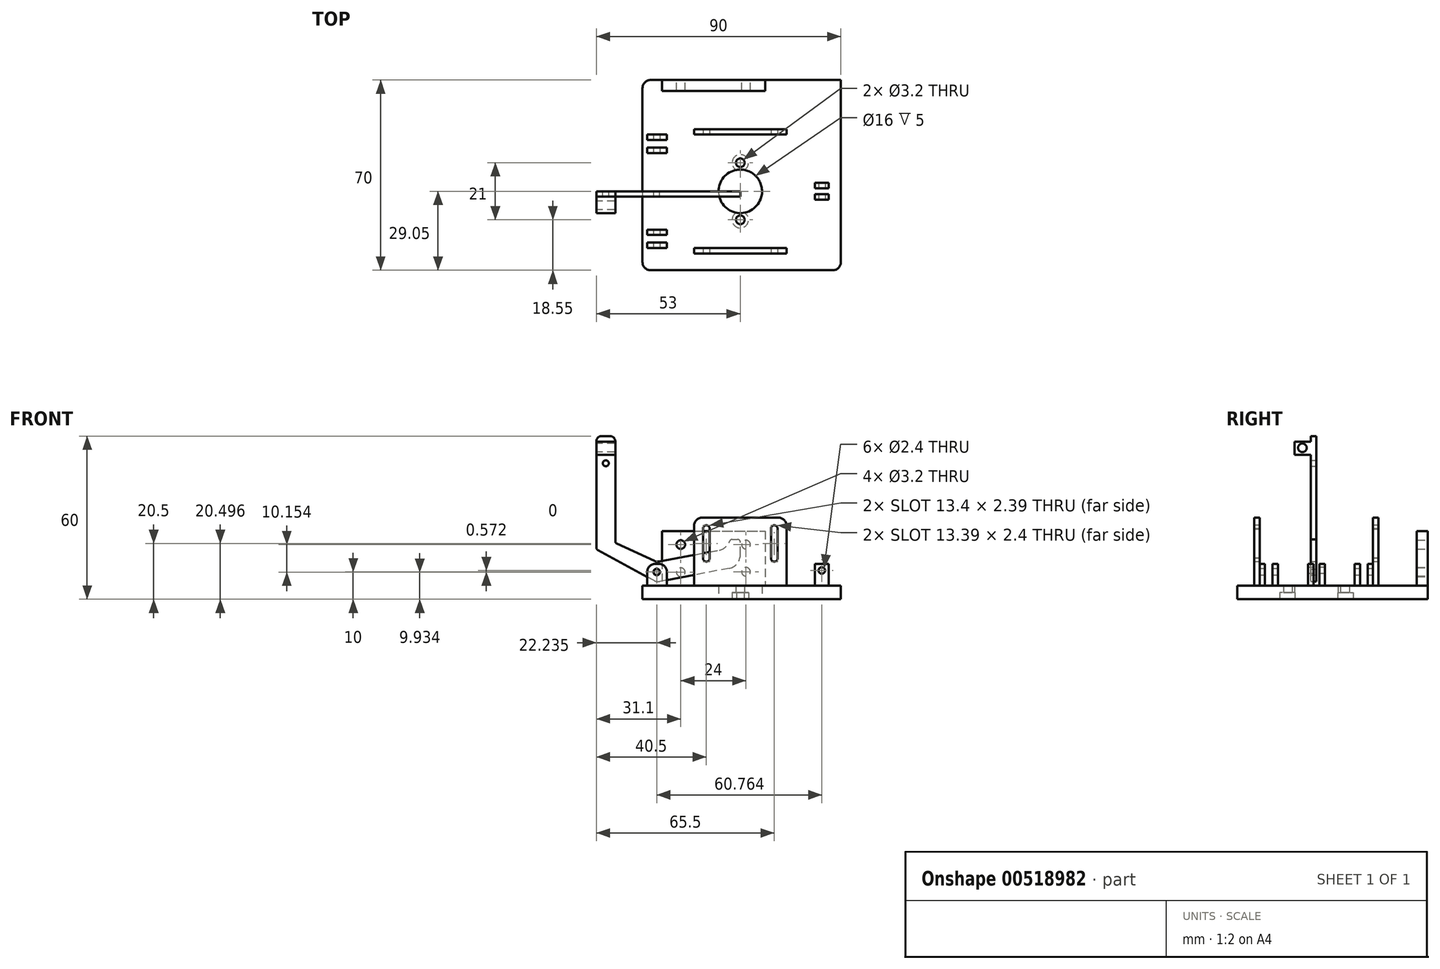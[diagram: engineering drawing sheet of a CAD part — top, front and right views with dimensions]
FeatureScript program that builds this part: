
annotation { "Feature Type Name" : "Feature", "Feature Type Description" : "" }
export const myFeature = defineFeature(function(context is Context, id is Id, definition is map)
    precondition{}
    {
        {
            var Q0;
            Q0=qCreatedBy(makeId("Top.planeOp"),FACE);
            var sketch = newSketch(context, id + "F0", { "sketchPlane" : qUnion([Q0])});
            skLineSegment(sketch, "E0.bottom", {"start": v(-36, 40.95) * mm, "end": v(37, 40.95) * mm});
            skLineSegment(sketch, "E0.top", {"start": v(-36, -29.05) * mm, "end": v(37, -29.05) * mm});
            skLineSegment(sketch, "E0.left", {"start": v(-36, 40.95) * mm, "end": v(-36, -29.05) * mm});
            skLineSegment(sketch, "E0.right", {"start": v(37, 40.95) * mm, "end": v(37, -29.05) * mm});
            skCircle(sketch, "E1.cCircle", {"center": v(0, 22.5) * mm, "radius": 2.85 * mm, "construction": true});
            skLineSegment(sketch, "E1.0", {"start": v(2.85, 20.85) * mm, "end": v(0, 19.2) * mm});
            skLineSegment(sketch, "E1.1", {"start": v(0, 19.2) * mm, "end": v(-2.85, 20.85) * mm});
            skLineSegment(sketch, "E1.2", {"start": v(-2.85, 20.85) * mm, "end": v(-2.85, 24.15) * mm});
            skLineSegment(sketch, "E1.3", {"start": v(-2.85, 24.15) * mm, "end": v(0, 25.8) * mm});
            skLineSegment(sketch, "E1.4", {"start": v(0, 25.8) * mm, "end": v(2.85, 24.15) * mm});
            skLineSegment(sketch, "E1.5", {"start": v(2.85, 24.15) * mm, "end": v(2.85, 20.85) * mm});
            skPoint(sketch, "E1.0.midPoint", {"position": v(1.43, 20.03) * mm});
            skCircle(sketch, "E2.cCircle", {"center": v(0, -22.5) * mm, "radius": 2.85 * mm, "construction": true});
            skLineSegment(sketch, "E2.0", {"start": v(2.85, -24.15) * mm, "end": v(0, -25.8) * mm});
            skLineSegment(sketch, "E2.1", {"start": v(0, -25.8) * mm, "end": v(-2.85, -24.15) * mm});
            skLineSegment(sketch, "E2.2", {"start": v(-2.85, -24.15) * mm, "end": v(-2.85, -20.85) * mm});
            skLineSegment(sketch, "E2.3", {"start": v(-2.85, -20.85) * mm, "end": v(0, -19.2) * mm});
            skLineSegment(sketch, "E2.4", {"start": v(0, -19.2) * mm, "end": v(2.85, -20.85) * mm});
            skLineSegment(sketch, "E2.5", {"start": v(2.85, -20.85) * mm, "end": v(2.85, -24.15) * mm});
            skPoint(sketch, "E2.0.midPoint", {"position": v(1.43, -24.97) * mm});
            skCircle(sketch, "E3", {"center": v(0, 22.5) * mm, "radius": 1.6 * mm});
            skCircle(sketch, "E4", {"center": v(0, -22.5) * mm, "radius": 1.6 * mm});
            skCircle(sketch, "E5", {"center": v(0, 0) * mm, "radius": 8 * mm});
            skLineSegment(sketch, "E6", {"start": v(0, 22.5) * mm, "end": v(0, 0) * mm, "construction": true});
            skLineSegment(sketch, "E7", {"start": v(0, 0) * mm, "end": v(0, -22.5) * mm, "construction": true});
            skCircle(sketch, "E8", {"center": v(0, 10.5) * mm, "radius": 3 * mm});
            skCircle(sketch, "E9", {"center": v(0, -10.5) * mm, "radius": 3 * mm});
            skPoint(sketch, "E10", {"position": v(0, 11.25) * mm});
            skCircle(sketch, "E11", {"center": v(0, 10.5) * mm, "radius": 1.6 * mm});
            skCircle(sketch, "E12", {"center": v(0, -10.5) * mm, "radius": 1.6 * mm});
            skLineSegment(sketch, "E13.bottom", {"start": v(17, 20.85) * mm, "end": v(-17, 20.85) * mm});
            skLineSegment(sketch, "E13.top", {"start": v(17, 22.85) * mm, "end": v(-17, 22.85) * mm});
            skLineSegment(sketch, "E13.left", {"start": v(17, 20.85) * mm, "end": v(17, 22.85) * mm});
            skLineSegment(sketch, "E13.right", {"start": v(-17, 20.85) * mm, "end": v(-17, 22.85) * mm});
            skLineSegment(sketch, "E14.bottom", {"start": v(17, -22.9) * mm, "end": v(-17, -22.9) * mm});
            skLineSegment(sketch, "E14.top", {"start": v(17, -20.9) * mm, "end": v(-17, -20.9) * mm});
            skLineSegment(sketch, "E14.left", {"start": v(17, -22.9) * mm, "end": v(17, -20.9) * mm});
            skLineSegment(sketch, "E14.right", {"start": v(-17, -22.9) * mm, "end": v(-17, -20.9) * mm});
            skLineSegment(sketch, "E15", {"start": v(0, -22.5) * mm, "end": v(17, -22.5) * mm, "construction": true});
            skLineSegment(sketch, "E16", {"start": v(0, -22.5) * mm, "end": v(-17, -22.5) * mm, "construction": true});
            skSolve(sketch);
        }
        {
            var Q0;
            Q0=makeQuery(id+"F0.imprint","IMPRINT",FACE,{"disambiguationData":[TD([[makeQuery(id+"F0.imprint","IMPRINT",EDGE,{"derivedFrom":sQuery(id+"F0.wireOp",EDGE,"E0.bottom")}),-1.0]])]});
            var Q1;
            Q1=makeQuery(id+"F0.imprint","IMPRINT",FACE,{"disambiguationData":[TD([[makeQuery(id+"F0.imprint","IMPRINT",EDGE,{"derivedFrom":sQuery(id+"F0.wireOp",EDGE,"E1.0")}),-1.0]])]});
            var Q2;
            Q2=makeQuery(id+"F0.imprint","IMPRINT",FACE,{"disambiguationData":[TD([[makeQuery(id+"F0.imprint","IMPRINT",EDGE,{"derivedFrom":sQuery(id+"F0.wireOp",EDGE,"E11")}),-1.0]])]});
            var Q3;
            Q3=makeQuery(id+"F0.imprint","IMPRINT",FACE,{"disambiguationData":[TD([[makeQuery(id+"F0.imprint","IMPRINT",EDGE,{"derivedFrom":sQuery(id+"F0.wireOp",EDGE,"E12")}),-1.0]])]});
            var Q4;
            {var subQ5=sQuery(id+"F0.wireOp",EDGE,"E13.right");Q4=makeQuery(id+"F0.imprint","IMPRINT",FACE,{"disambiguationData":[TD([[makeQuery(id+"F0.imprint","IMPRINT",EDGE,{"derivedFrom":subQ5}),-1.0]])]});}
            var Q5;
            {var subQ5=sQuery(id+"F0.wireOp",EDGE,"E13.left");Q5=makeQuery(id+"F0.imprint","IMPRINT",FACE,{"disambiguationData":[TD([[makeQuery(id+"F0.imprint","IMPRINT",EDGE,{"derivedFrom":subQ5}),1.0]])]});}
            var Q6;
            {var subQ5=sQuery(id+"F0.wireOp",EDGE,"E13.top");var subQ6=sQuery(id+"F0.wireOp",EDGE,"E3");var subQ7=makeQuery(id+"F0.imprint","INTERSECT",VERTEX,{"disambiguationData":[OD(0.0)],"derivedFrom":[subQ6,subQ5]});Q6=makeQuery(id+"F0.imprint","IMPRINT",FACE,{"disambiguationData":[TD([[makeQuery(id+"F0.imprint","IMPRINT",EDGE,{"disambiguationData":[TD([[subQ7,1.0]])],"derivedFrom":subQ6}),-1.0]])]});}
            var Q7;
            {var subQ0=sQuery(id+"F0.wireOp",EDGE,"E13.top");var subQ1=sQuery(id+"F0.wireOp",EDGE,"E3");var subQ2=makeQuery(id+"F0.imprint","INTERSECT",VERTEX,{"disambiguationData":[OD(0.0)],"derivedFrom":[subQ1,subQ0]});Q7=makeQuery(id+"F0.imprint","IMPRINT",FACE,{"disambiguationData":[TD([[makeQuery(id+"F0.imprint","IMPRINT",EDGE,{"disambiguationData":[TD([[subQ2,1.0]])],"derivedFrom":subQ1}),1.0]])]});}
            var Q8;
            {var subQ5=sQuery(id+"F0.wireOp",EDGE,"E14.right");Q8=makeQuery(id+"F0.imprint","IMPRINT",FACE,{"disambiguationData":[TD([[makeQuery(id+"F0.imprint","IMPRINT",EDGE,{"derivedFrom":subQ5}),-1.0]])]});}
            var Q9;
            {var subQ0=sQuery(id+"F0.wireOp",EDGE,"E14.bottom");var subQ8=sQuery(id+"F0.wireOp",EDGE,"E2.2");var subQ9=makeQuery(id+"F0.imprint","INTERSECT",VERTEX,{"derivedFrom":[subQ8,subQ0]});Q9=makeQuery(id+"F0.imprint","IMPRINT",FACE,{"disambiguationData":[TD([[makeQuery(id+"F0.imprint","IMPRINT",EDGE,{"disambiguationData":[TD([[subQ9,-1.0]])],"derivedFrom":subQ8}),-1.0]])]});}
            var Q10;
            {var subQ0=sQuery(id+"F0.wireOp",EDGE,"E14.bottom");var subQ1=sQuery(id+"F0.wireOp",EDGE,"E4");var subQ2=makeQuery(id+"F0.imprint","INTERSECT",VERTEX,{"disambiguationData":[OD(0.0)],"derivedFrom":[subQ1,subQ0]});Q10=makeQuery(id+"F0.imprint","IMPRINT",FACE,{"disambiguationData":[TD([[makeQuery(id+"F0.imprint","IMPRINT",EDGE,{"disambiguationData":[TD([[subQ2,-1.0]])],"derivedFrom":subQ1}),1.0]])]});}
            var Q11;
            {var subQ6=sQuery(id+"F0.wireOp",EDGE,"E2.3");Q11=makeQuery(id+"F0.imprint","IMPRINT",FACE,{"disambiguationData":[TD([[makeQuery(id+"F0.imprint","IMPRINT",EDGE,{"derivedFrom":subQ6}),-1.0]])]});}
            var Q12;
            {var subQ5=sQuery(id+"F0.wireOp",EDGE,"E14.left");Q12=makeQuery(id+"F0.imprint","IMPRINT",FACE,{"disambiguationData":[TD([[makeQuery(id+"F0.imprint","IMPRINT",EDGE,{"derivedFrom":subQ5}),1.0]])]});}
            var Q13;
            {var subQ0=sQuery(id+"F0.wireOp",EDGE,"E14.bottom");var subQ1=sQuery(id+"F0.wireOp",EDGE,"E4");var subQ2=makeQuery(id+"F0.imprint","INTERSECT",VERTEX,{"disambiguationData":[OD(0.0)],"derivedFrom":[subQ1,subQ0]});Q13=makeQuery(id+"F0.imprint","IMPRINT",FACE,{"disambiguationData":[TD([[makeQuery(id+"F0.imprint","IMPRINT",EDGE,{"disambiguationData":[TD([[subQ2,1.0]])],"derivedFrom":subQ1}),1.0]])]});}
            var Q14;
            {var subQ8=sQuery(id+"F0.wireOp",EDGE,"E1.3");Q14=makeQuery(id+"F0.imprint","IMPRINT",FACE,{"disambiguationData":[TD([[makeQuery(id+"F0.imprint","IMPRINT",EDGE,{"derivedFrom":subQ8}),-1.0]])]});}
            var Q15;
            {var subQ0=sQuery(id+"F0.wireOp",EDGE,"E13.top");var subQ1=sQuery(id+"F0.wireOp",EDGE,"E3");var subQ2=makeQuery(id+"F0.imprint","INTERSECT",VERTEX,{"disambiguationData":[OD(0.0)],"derivedFrom":[subQ1,subQ0]});Q15=makeQuery(id+"F0.imprint","IMPRINT",FACE,{"disambiguationData":[TD([[makeQuery(id+"F0.imprint","IMPRINT",EDGE,{"disambiguationData":[TD([[subQ2,-1.0]])],"derivedFrom":subQ1}),1.0]])]});}
            var Q16;
            {var subQ1=sQuery(id+"F0.wireOp",EDGE,"E2.0");Q16=makeQuery(id+"F0.imprint","IMPRINT",FACE,{"disambiguationData":[TD([[makeQuery(id+"F0.imprint","IMPRINT",EDGE,{"derivedFrom":subQ1}),-1.0]])]});}
            extrude(context, id + "F1", {"entities" : qUnion([Q0, Q1, Q2, Q3, Q4, Q5, Q6, Q7, Q8, Q9, Q10, Q11, Q12, Q13, Q14, Q15, Q16]), "depth" : 5 * mm, "offsetDistance" : 25 * mm});
        }
        {
            var Q0;
            Q0=makeQuery(id+"F0.imprint","IMPRINT",FACE,{"disambiguationData":[TD([[makeQuery(id+"F0.imprint","IMPRINT",EDGE,{"derivedFrom":sQuery(id+"F0.wireOp",EDGE,"E11")}),-1.0]])]});
            var Q1;
            Q1=makeQuery(id+"F0.imprint","IMPRINT",FACE,{"disambiguationData":[TD([[makeQuery(id+"F0.imprint","IMPRINT",EDGE,{"derivedFrom":sQuery(id+"F0.wireOp",EDGE,"E12")}),-1.0]])]});
            extrude(context, id + "F2", {"entities" : qUnion([Q0, Q1]), "operationType" : NewBodyOperationType.REMOVE, "depth" : 2.5 * mm, "offsetDistance" : 25 * mm});
        }
        {
            var Q0;
            {var subQ5=sQuery(id+"F0.wireOp",EDGE,"E14.right");Q0=makeQuery(id+"F0.imprint","IMPRINT",FACE,{"disambiguationData":[TD([[makeQuery(id+"F0.imprint","IMPRINT",EDGE,{"derivedFrom":subQ5}),-1.0]])]});}
            var Q1;
            {var subQ0=sQuery(id+"F0.wireOp",EDGE,"E14.bottom");var subQ8=sQuery(id+"F0.wireOp",EDGE,"E2.2");var subQ9=makeQuery(id+"F0.imprint","INTERSECT",VERTEX,{"derivedFrom":[subQ8,subQ0]});Q1=makeQuery(id+"F0.imprint","IMPRINT",FACE,{"disambiguationData":[TD([[makeQuery(id+"F0.imprint","IMPRINT",EDGE,{"disambiguationData":[TD([[subQ9,-1.0]])],"derivedFrom":subQ8}),-1.0]])]});}
            var Q2;
            {var subQ0=sQuery(id+"F0.wireOp",EDGE,"E14.bottom");var subQ1=sQuery(id+"F0.wireOp",EDGE,"E4");var subQ2=makeQuery(id+"F0.imprint","INTERSECT",VERTEX,{"disambiguationData":[OD(0.0)],"derivedFrom":[subQ1,subQ0]});Q2=makeQuery(id+"F0.imprint","IMPRINT",FACE,{"disambiguationData":[TD([[makeQuery(id+"F0.imprint","IMPRINT",EDGE,{"disambiguationData":[TD([[subQ2,-1.0]])],"derivedFrom":subQ1}),1.0]])]});}
            var Q3;
            {var subQ5=sQuery(id+"F0.wireOp",EDGE,"E14.left");Q3=makeQuery(id+"F0.imprint","IMPRINT",FACE,{"disambiguationData":[TD([[makeQuery(id+"F0.imprint","IMPRINT",EDGE,{"derivedFrom":subQ5}),1.0]])]});}
            var Q4;
            {var subQ5=sQuery(id+"F0.wireOp",EDGE,"E13.right");Q4=makeQuery(id+"F0.imprint","IMPRINT",FACE,{"disambiguationData":[TD([[makeQuery(id+"F0.imprint","IMPRINT",EDGE,{"derivedFrom":subQ5}),-1.0]])]});}
            var Q5;
            {var subQ5=sQuery(id+"F0.wireOp",EDGE,"E13.top");var subQ6=sQuery(id+"F0.wireOp",EDGE,"E3");var subQ7=makeQuery(id+"F0.imprint","INTERSECT",VERTEX,{"disambiguationData":[OD(0.0)],"derivedFrom":[subQ6,subQ5]});Q5=makeQuery(id+"F0.imprint","IMPRINT",FACE,{"disambiguationData":[TD([[makeQuery(id+"F0.imprint","IMPRINT",EDGE,{"disambiguationData":[TD([[subQ7,1.0]])],"derivedFrom":subQ6}),-1.0]])]});}
            var Q6;
            {var subQ0=sQuery(id+"F0.wireOp",EDGE,"E13.top");var subQ1=sQuery(id+"F0.wireOp",EDGE,"E3");var subQ2=makeQuery(id+"F0.imprint","INTERSECT",VERTEX,{"disambiguationData":[OD(0.0)],"derivedFrom":[subQ1,subQ0]});Q6=makeQuery(id+"F0.imprint","IMPRINT",FACE,{"disambiguationData":[TD([[makeQuery(id+"F0.imprint","IMPRINT",EDGE,{"disambiguationData":[TD([[subQ2,1.0]])],"derivedFrom":subQ1}),1.0]])]});}
            var Q7;
            {var subQ5=sQuery(id+"F0.wireOp",EDGE,"E13.left");Q7=makeQuery(id+"F0.imprint","IMPRINT",FACE,{"disambiguationData":[TD([[makeQuery(id+"F0.imprint","IMPRINT",EDGE,{"derivedFrom":subQ5}),1.0]])]});}
            extrude(context, id + "F3", {"entities" : qUnion([Q0, Q1, Q2, Q3, Q4, Q5, Q6, Q7]), "operationType" : NewBodyOperationType.ADD, "depth" : 30 * mm, "offsetDistance" : 25 * mm});
        }
        {
            var Q0;
            Q0=makeQuery(id+"F3.opExtrude","SWEPT_FACE",FACE,{"disambiguationData":[OSD([sQuery(id+"F0.wireOp",EDGE,"E14.bottom")])]});
            var sketch = newSketch(context, id + "F4", { "sketchPlane" : qUnion([Q0])});
            skCircle(sketch, "E17", {"center": v(-12.5, 26) * mm, "radius": 1.2 * mm});
            skCircle(sketch, "E18", {"center": v(-12.5, 15) * mm, "radius": 1.2 * mm});
            skCircle(sketch, "E19", {"center": v(12.5, 15) * mm, "radius": 1.2 * mm});
            skCircle(sketch, "E20", {"center": v(12.5, 26) * mm, "radius": 1.2 * mm});
            skLineSegment(sketch, "E21", {"start": v(-13.7, 25.89) * mm, "end": v(-13.7, 14.89) * mm});
            skLineSegment(sketch, "E22", {"start": v(-13.7, 14.89) * mm, "end": v(-11.3, 14.89) * mm});
            skLineSegment(sketch, "E23", {"start": v(-11.3, 14.89) * mm, "end": v(-11.3, 25.89) * mm});
            skLineSegment(sketch, "E24", {"start": v(-11.3, 25.89) * mm, "end": v(-13.7, 25.89) * mm});
            skLineSegment(sketch, "E25", {"start": v(11.3, 15.05) * mm, "end": v(11.3, 26) * mm});
            skLineSegment(sketch, "E26", {"start": v(13.67, 26.28) * mm, "end": v(13.7, 15) * mm});
            skLineSegment(sketch, "E27", {"start": v(12.5, 15) * mm, "end": v(17, 15) * mm, "construction": true});
            skLineSegment(sketch, "E28", {"start": v(-12.5, 15) * mm, "end": v(-17, 15) * mm, "construction": true});
            skSolve(sketch);
        }
        {
            var Q0;
            Q0 = qSketchRegion(id + "F4", true);
            extrude(context, id + "F5", {"entities" : qUnion([Q0]), "operationType" : NewBodyOperationType.REMOVE, "oppositeDirection" : true, "depth" : 60 * mm, "offsetDistance" : 25 * mm});
        }
        {
            var Q0;
            Q0=makeQuery(id+"F1.opExtrude","CAP_FACE",FACE,{"disambiguationData":[OSD([sQuery(id+"F0.wireOp",EDGE,"E0.bottom"),sQuery(id+"F0.wireOp",EDGE,"E0.top"),sQuery(id+"F0.wireOp",EDGE,"E0.left"),sQuery(id+"F0.wireOp",EDGE,"E0.right"),sQuery(id+"F0.wireOp",EDGE,"E5"),sQuery(id+"F0.wireOp",EDGE,"E11"),sQuery(id+"F0.wireOp",EDGE,"E12")])],"isStart":false});
            var sketch = newSketch(context, id + "F6", { "sketchPlane" : qUnion([Q0])});
            skLineSegment(sketch, "E29.bottom", {"start": v(-27, 20.85) * mm, "end": v(-34.26, 20.85) * mm});
            skLineSegment(sketch, "E29.top", {"start": v(-27, 18.85) * mm, "end": v(-34.26, 18.85) * mm});
            skLineSegment(sketch, "E29.left", {"start": v(-27, 20.85) * mm, "end": v(-27, 18.85) * mm});
            skLineSegment(sketch, "E29.right", {"start": v(-34.26, 20.85) * mm, "end": v(-34.26, 18.85) * mm});
            skLineSegment(sketch, "E30.bottom", {"start": v(-27, 16.05) * mm, "end": v(-34.26, 16.05) * mm});
            skLineSegment(sketch, "E30.top", {"start": v(-27, 14.05) * mm, "end": v(-34.26, 14.05) * mm});
            skLineSegment(sketch, "E30.left", {"start": v(-27, 16.05) * mm, "end": v(-27, 14.05) * mm});
            skLineSegment(sketch, "E30.right", {"start": v(-34.26, 16.05) * mm, "end": v(-34.26, 14.05) * mm});
            skLineSegment(sketch, "E31.bottom", {"start": v(-34.26, -14.1) * mm, "end": v(-27, -14.1) * mm});
            skLineSegment(sketch, "E31.top", {"start": v(-34.26, -16.1) * mm, "end": v(-27, -16.1) * mm});
            skLineSegment(sketch, "E31.left", {"start": v(-34.26, -14.1) * mm, "end": v(-34.26, -16.1) * mm});
            skLineSegment(sketch, "E31.right", {"start": v(-27, -14.1) * mm, "end": v(-27, -16.1) * mm});
            skLineSegment(sketch, "E32.bottom", {"start": v(-27, -18.9) * mm, "end": v(-34.26, -18.9) * mm});
            skLineSegment(sketch, "E32.top", {"start": v(-27, -20.9) * mm, "end": v(-34.26, -20.9) * mm});
            skLineSegment(sketch, "E32.left", {"start": v(-27, -18.9) * mm, "end": v(-27, -20.9) * mm});
            skLineSegment(sketch, "E32.right", {"start": v(-34.26, -18.9) * mm, "end": v(-34.26, -20.9) * mm});
            skLineSegment(sketch, "E33", {"start": v(-34.26, -16.1) * mm, "end": v(-34.26, -18.9) * mm, "construction": true});
            skLineSegment(sketch, "E34", {"start": v(-34.26, 18.85) * mm, "end": v(-34.26, 16.05) * mm, "construction": true});
            skLineSegment(sketch, "E35.bottom", {"start": v(27.5, 3.1) * mm, "end": v(32.5, 3.1) * mm});
            skLineSegment(sketch, "E35.top", {"start": v(27.5, 1.1) * mm, "end": v(32.5, 1.1) * mm});
            skLineSegment(sketch, "E35.left", {"start": v(27.5, 3.1) * mm, "end": v(27.5, 1.1) * mm});
            skLineSegment(sketch, "E35.right", {"start": v(32.5, 3.1) * mm, "end": v(32.5, 1.1) * mm});
            skLineSegment(sketch, "E36.bottom", {"start": v(27.5, -1.1) * mm, "end": v(32.5, -1.1) * mm});
            skLineSegment(sketch, "E36.top", {"start": v(27.5, -3.1) * mm, "end": v(32.5, -3.1) * mm});
            skLineSegment(sketch, "E36.left", {"start": v(27.5, -1.1) * mm, "end": v(27.5, -3.1) * mm});
            skLineSegment(sketch, "E36.right", {"start": v(32.5, -1.1) * mm, "end": v(32.5, -3.1) * mm});
            skSolve(sketch);
        }
        {
            var Q0;
            Q0=makeQuery(id+"F6.imprint","IMPRINT",FACE,{"disambiguationData":[TD([[makeQuery(id+"F6.imprint","IMPRINT",EDGE,{"derivedFrom":sQuery(id+"F6.wireOp",EDGE,"E29.bottom")}),1.0]])]});
            var Q1;
            Q1=makeQuery(id+"F6.imprint","IMPRINT",FACE,{"disambiguationData":[TD([[makeQuery(id+"F6.imprint","IMPRINT",EDGE,{"derivedFrom":sQuery(id+"F6.wireOp",EDGE,"E30.bottom")}),1.0]])]});
            var Q2;
            Q2=makeQuery(id+"F6.imprint","IMPRINT",FACE,{"disambiguationData":[TD([[makeQuery(id+"F6.imprint","IMPRINT",EDGE,{"derivedFrom":sQuery(id+"F6.wireOp",EDGE,"E31.bottom")}),-1.0]])]});
            var Q3;
            Q3=makeQuery(id+"F6.imprint","IMPRINT",FACE,{"disambiguationData":[TD([[makeQuery(id+"F6.imprint","IMPRINT",EDGE,{"derivedFrom":sQuery(id+"F6.wireOp",EDGE,"E32.bottom")}),1.0]])]});
            var Q4;
            Q4=makeQuery(id+"F6.imprint","IMPRINT",FACE,{"disambiguationData":[TD([[makeQuery(id+"F6.imprint","IMPRINT",EDGE,{"derivedFrom":sQuery(id+"F6.wireOp",EDGE,"E35.bottom")}),-1.0]])]});
            var Q5;
            Q5=makeQuery(id+"F6.imprint","IMPRINT",FACE,{"disambiguationData":[TD([[makeQuery(id+"F6.imprint","IMPRINT",EDGE,{"derivedFrom":sQuery(id+"F6.wireOp",EDGE,"E36.bottom")}),-1.0]])]});
            extrude(context, id + "F7", {"entities" : qUnion([Q0, Q1, Q2, Q3, Q4, Q5]), "operationType" : NewBodyOperationType.ADD, "depth" : 8 * mm, "offsetDistance" : 25 * mm});
        }
        {
            var Q0;
            Q0=makeQuery(id+"F7.opExtrude","SWEPT_FACE",FACE,{"disambiguationData":[OSD([sQuery(id+"F6.wireOp",EDGE,"E32.top")])]});
            var sketch = newSketch(context, id + "F8", { "sketchPlane" : qUnion([Q0])});
            skCircle(sketch, "E37", {"center": v(-30.76, 10) * mm, "radius": 1.2 * mm});
            skCircle(sketch, "E38", {"center": v(30, 10.57) * mm, "radius": 1.2 * mm});
            skSolve(sketch);
        }
        {
            var Q0;
            Q0=makeQuery(id+"F8.imprint","IMPRINT",FACE,{"disambiguationData":[TD([[makeQuery(id+"F8.imprint","IMPRINT",EDGE,{"derivedFrom":sQuery(id+"F8.wireOp",EDGE,"E37")}),1.0]])]});
            var Q1;
            Q1=makeQuery(id+"F8.imprint","IMPRINT",FACE,{"disambiguationData":[TD([[makeQuery(id+"F8.imprint","IMPRINT",EDGE,{"derivedFrom":sQuery(id+"F8.wireOp",EDGE,"E38")}),1.0]])]});
            extrude(context, id + "F9", {"entities" : qUnion([Q0, Q1]), "operationType" : NewBodyOperationType.REMOVE, "oppositeDirection" : true, "depth" : 60 * mm, "offsetDistance" : 25 * mm});
        }
        {
            var Q0;
            Q0=qCreatedBy(makeId("Front.planeOp"),FACE);
            var sketch = newSketch(context, id + "F10", { "sketchPlane" : qUnion([Q0])});
            skLineSegment(sketch, "E39", {"start": v(0, 12.14) * mm, "end": v(-29.71, 6.51) * mm});
            skLineSegment(sketch, "E40", {"start": v(-31.7, 6.82) * mm, "end": v(-53, 18.4) * mm});
            skLineSegment(sketch, "E41", {"start": v(-53, 18.4) * mm, "end": v(-53, 58) * mm});
            skLineSegment(sketch, "E42", {"start": v(-51, 60) * mm, "end": v(-48, 60) * mm});
            skLineSegment(sketch, "E43", {"start": v(-46, 58) * mm, "end": v(-46, 20.68) * mm});
            skLineSegment(sketch, "E44", {"start": v(-46, 20.68) * mm, "end": v(-31.63, 14.09) * mm});
            skLineSegment(sketch, "E45", {"start": v(-29.82, 13.86) * mm, "end": v(-4, 18.75) * mm});
            skLineSegment(sketch, "E46", {"start": v(-4, 18.75) * mm, "end": v(-4, 22) * mm});
            skLineSegment(sketch, "E47", {"start": v(-4, 22) * mm, "end": v(0, 22) * mm});
            skLineSegment(sketch, "E48", {"start": v(0, 12.14) * mm, "end": v(0, 22) * mm});
            skCircle(sketch, "E49", {"center": v(-30.76, 10) * mm, "radius": 1.1 * mm});
            skPoint(sketch, "E50.visualSharp", {"position": v(-46, 60) * mm});
            skArc(sketch, "E50.filletArc", {"start": v(-46, 58) * mm, "mid": v(-46.59, 59.41) * mm, "end": v(-48, 60) * mm});
            skPoint(sketch, "E51.visualSharp", {"position": v(-53, 60) * mm});
            skArc(sketch, "E51.filletArc", {"start": v(-51, 60) * mm, "mid": v(-52.41, 59.41) * mm, "end": v(-53, 58) * mm});
            skCircle(sketch, "E52", {"center": v(-49.5, 50) * mm, "radius": 1.1 * mm});
            skPoint(sketch, "E52.centerSnap0", {"position": v(-49.5, 60) * mm});
            skLineSegment(sketch, "E53", {"start": v(-30.76, 10) * mm, "end": v(-30.76, 13.69) * mm, "construction": true});
            skLineSegment(sketch, "E54", {"start": v(-30.76, 10) * mm, "end": v(-30.76, 6.31) * mm, "construction": true});
            skPoint(sketch, "E55.visualSharp", {"position": v(-30.76, 6.31) * mm});
            skArc(sketch, "E55.filletArc", {"start": v(-31.7, 6.82) * mm, "mid": v(-30.74, 6.5) * mm, "end": v(-29.71, 6.51) * mm});
            skPoint(sketch, "E56.visualSharp", {"position": v(-30.76, 13.69) * mm});
            skArc(sketch, "E56.filletArc", {"start": v(-31.63, 14.09) * mm, "mid": v(-30.75, 13.83) * mm, "end": v(-29.82, 13.86) * mm});
            skLineSegment(sketch, "E57", {"start": v(-53, 53.14) * mm, "end": v(-46, 53.14) * mm});
            skLineSegment(sketch, "E58", {"start": v(-46, 53.14) * mm, "end": v(-46, 58) * mm});
            skLineSegment(sketch, "E59", {"start": v(-53, 58) * mm, "end": v(-53, 53.14) * mm});
            skLineSegment(sketch, "E60", {"start": v(-53, 58) * mm, "end": v(-46, 58) * mm});
            skSolve(sketch);
        }
        {
            var Q0;
            Q0=makeQuery(id+"F10.imprint","IMPRINT",FACE,{"disambiguationData":[TD([[makeQuery(id+"F10.imprint","IMPRINT",EDGE,{"derivedFrom":sQuery(id+"F10.wireOp",EDGE,"E39")}),-1.0]])]});
            var Q1;
            Q1=makeQuery(id+"F10.imprint","IMPRINT",FACE,{"disambiguationData":[TD([[makeQuery(id+"F10.imprint","IMPRINT",EDGE,{"derivedFrom":sQuery(id+"F10.wireOp",EDGE,"E42")}),-1.0]])]});
            var Q2;
            Q2=makeQuery(id+"F10.imprint","IMPRINT",FACE,{"disambiguationData":[TD([[makeQuery(id+"F10.imprint","IMPRINT",EDGE,{"derivedFrom":sQuery(id+"F10.wireOp",EDGE,"E57")}),1.0]])]});
            extrude(context, id + "F11", {"entities" : qUnion([Q0, Q1, Q2]), "depth" : 2 * mm, "offsetDistance" : 25 * mm});
        }
        {
            var Q0;
            Q0=makeQuery(id+"F11.opExtrude","SWEPT_EDGE",EDGE,{"disambiguationData":[OSD([sQuery(id+"F10.wireOp",EDGE,"E42"),sQuery(id+"F10.wireOp",EDGE,"E43")])]});
            var Q1;
            Q1=makeQuery(id+"F11.opExtrude","SWEPT_EDGE",EDGE,{"disambiguationData":[OSD([sQuery(id+"F10.wireOp",EDGE,"E41"),sQuery(id+"F10.wireOp",EDGE,"E42")])]});
            var Q2;
            Q2=makeQuery(id+"F11.opExtrude","SWEPT_EDGE",EDGE,{"disambiguationData":[OSD([sQuery(id+"F10.wireOp",EDGE,"E46"),sQuery(id+"F10.wireOp",EDGE,"E47")])]});
            var Q3;
            Q3=makeQuery(id+"F11.opExtrude","SWEPT_EDGE",EDGE,{"disambiguationData":[OSD([sQuery(id+"F10.wireOp",EDGE,"E47"),sQuery(id+"F10.wireOp",EDGE,"E48")])]});
            fillet(context, id + "F12", {"entities" : qUnion([Q0, Q1, Q2, Q3]), "radius" : 1 * mm, "tangentPropagation" : true, "allowEdgeOverflow" : false});
        }
        {
            var Q0;
            Q0=makeQuery(id+"F11.opExtrude","SWEPT_EDGE",EDGE,{"disambiguationData":[OSD([sQuery(id+"F10.wireOp",EDGE,"E40"),sQuery(id+"F10.wireOp",EDGE,"E41")])]});
            var Q1;
            Q1=makeQuery(id+"F11.opExtrude","SWEPT_EDGE",EDGE,{"disambiguationData":[OSD([sQuery(id+"F10.wireOp",EDGE,"E39"),sQuery(id+"F10.wireOp",EDGE,"E40")])]});
            var Q2;
            Q2=makeQuery(id+"F11.opExtrude","SWEPT_EDGE",EDGE,{"disambiguationData":[OSD([sQuery(id+"F10.wireOp",EDGE,"E44"),sQuery(id+"F10.wireOp",EDGE,"E45")])]});
            fillet(context, id + "F13", {"entities" : qUnion([Q0, Q1, Q2]), "radius" : 5 * mm, "tangentPropagation" : true, "allowEdgeOverflow" : false});
        }
        {
            var Q0;
            Q0=makeQuery(id+"F7.opExtrude","CAP_EDGE",EDGE,{"disambiguationData":[OSD([sQuery(id+"F6.wireOp",EDGE,"E30.right")])],"isStart":false});
            var Q1;
            Q1=makeQuery(id+"F7.opExtrude","CAP_EDGE",EDGE,{"disambiguationData":[OSD([sQuery(id+"F6.wireOp",EDGE,"E29.right")])],"isStart":false});
            var Q2;
            Q2=makeQuery(id+"F7.opExtrude","CAP_EDGE",EDGE,{"disambiguationData":[OSD([sQuery(id+"F6.wireOp",EDGE,"E32.left")])],"isStart":false});
            var Q3;
            Q3=makeQuery(id+"F7.opExtrude","CAP_EDGE",EDGE,{"disambiguationData":[OSD([sQuery(id+"F6.wireOp",EDGE,"E32.right")])],"isStart":false});
            var Q4;
            Q4=makeQuery(id+"F7.opExtrude","CAP_EDGE",EDGE,{"disambiguationData":[OSD([sQuery(id+"F6.wireOp",EDGE,"E31.left")])],"isStart":false});
            var Q5;
            Q5=makeQuery(id+"F7.opExtrude","CAP_EDGE",EDGE,{"disambiguationData":[OSD([sQuery(id+"F6.wireOp",EDGE,"E31.right")])],"isStart":false});
            var Q6;
            Q6=makeQuery(id+"F7.opExtrude","CAP_EDGE",EDGE,{"disambiguationData":[OSD([sQuery(id+"F6.wireOp",EDGE,"E30.left")])],"isStart":false});
            var Q7;
            Q7=makeQuery(id+"F7.opExtrude","CAP_EDGE",EDGE,{"disambiguationData":[OSD([sQuery(id+"F6.wireOp",EDGE,"E29.left")])],"isStart":false});
            var Q8;
            Q8=makeQuery(id+"F3.opExtrude","CAP_EDGE",EDGE,{"disambiguationData":[OSD([sQuery(id+"F0.wireOp",EDGE,"E13.right")])],"isStart":false});
            var Q9;
            Q9=makeQuery(id+"F3.opExtrude","CAP_EDGE",EDGE,{"disambiguationData":[OSD([sQuery(id+"F0.wireOp",EDGE,"E13.left")])],"isStart":false});
            var Q10;
            Q10=makeQuery(id+"F3.opExtrude","CAP_EDGE",EDGE,{"disambiguationData":[OSD([sQuery(id+"F0.wireOp",EDGE,"E14.right")])],"isStart":false});
            var Q11;
            Q11=makeQuery(id+"F3.opExtrude","CAP_EDGE",EDGE,{"disambiguationData":[OSD([sQuery(id+"F0.wireOp",EDGE,"E14.left")])],"isStart":false});
            var Q12;
            Q12=makeQuery(id+"F1.opExtrude","SWEPT_EDGE",EDGE,{"disambiguationData":[OSD([sQuery(id+"F0.wireOp",EDGE,"E0.top"),sQuery(id+"F0.wireOp",EDGE,"E0.right")])]});
            var Q13;
            Q13=makeQuery(id+"F1.opExtrude","SWEPT_EDGE",EDGE,{"disambiguationData":[OSD([sQuery(id+"F0.wireOp",EDGE,"E0.top"),sQuery(id+"F0.wireOp",EDGE,"E0.left")])]});
            var Q14;
            Q14=makeQuery(id+"F1.opExtrude","SWEPT_EDGE",EDGE,{"disambiguationData":[OSD([sQuery(id+"F0.wireOp",EDGE,"E0.bottom"),sQuery(id+"F0.wireOp",EDGE,"E0.left")])]});
            fillet(context, id + "F14", {"entities" : qUnion([Q0, Q1, Q2, Q3, Q4, Q5, Q6, Q7, Q8, Q9, Q10, Q11, Q12, Q13, Q14]), "radius" : 3 * mm, "tangentPropagation" : true, "allowEdgeOverflow" : false});
        }
        {
            var Q0;
            Q0=makeQuery(id+"F10.imprint","IMPRINT",FACE,{"disambiguationData":[TD([[makeQuery(id+"F10.imprint","IMPRINT",EDGE,{"derivedFrom":sQuery(id+"F10.wireOp",EDGE,"E57")}),1.0]])]});
            extrude(context, id + "F15", {"entities" : qUnion([Q0]), "operationType" : NewBodyOperationType.ADD, "depth" : 8 * mm, "offsetDistance" : 25 * mm});
        }
        {
            var Q0;
            {var subQ0=sQuery(id+"F10.wireOp",EDGE,"E59");Q0=makeQuery(id+"F15.boolean.opBoolean","MERGE",FACE,{"derivedFrom":[makeQuery(id+"F11.opExtrude","SWEPT_FACE",FACE,{"disambiguationData":[OSD([sQuery(id+"F10.wireOp",EDGE,"E41"),subQ0])]}),makeQuery(id+"F15.opExtrude","SWEPT_FACE",FACE,{"disambiguationData":[OSD([subQ0])]})]});}
            var sketch = newSketch(context, id + "F16", { "sketchPlane" : qUnion([Q0])});
            skCircle(sketch, "E61", {"center": v(5.16, 55.68) * mm, "radius": 1.6 * mm});
            skSolve(sketch);
        }
        {
            var Q0;
            Q0=makeQuery(id+"F16.imprint","IMPRINT",FACE,{"disambiguationData":[TD([[makeQuery(id+"F16.imprint","IMPRINT",EDGE,{"derivedFrom":sQuery(id+"F16.wireOp",EDGE,"E61")}),1.0]])]});
            extrude(context, id + "F17", {"entities" : qUnion([Q0]), "operationType" : NewBodyOperationType.REMOVE, "oppositeDirection" : true, "depth" : 25 * mm, "offsetDistance" : 25 * mm});
        }
        {
            var Q0;
            Q0=makeQuery(id+"F1.opExtrude","CAP_FACE",FACE,{"disambiguationData":[OSD([sQuery(id+"F0.wireOp",EDGE,"E0.bottom"),sQuery(id+"F0.wireOp",EDGE,"E0.top"),sQuery(id+"F0.wireOp",EDGE,"E0.left"),sQuery(id+"F0.wireOp",EDGE,"E0.right"),sQuery(id+"F0.wireOp",EDGE,"E5"),sQuery(id+"F0.wireOp",EDGE,"E11"),sQuery(id+"F0.wireOp",EDGE,"E12"),sQuery(id+"F0.wireOp",EDGE,"E13.left"),sQuery(id+"F0.wireOp",EDGE,"E14.left")])],"isStart":false});
            var sketch = newSketch(context, id + "F18", { "sketchPlane" : qUnion([Q0])});
            skLineSegment(sketch, "E62.bottom", {"start": v(-28.82, 40.95) * mm, "end": v(9.18, 40.95) * mm});
            skLineSegment(sketch, "E62.top", {"start": v(-28.82, 36.95) * mm, "end": v(9.18, 36.95) * mm});
            skLineSegment(sketch, "E62.left", {"start": v(-28.82, 40.95) * mm, "end": v(-28.82, 36.95) * mm});
            skLineSegment(sketch, "E62.right", {"start": v(9.18, 40.95) * mm, "end": v(9.18, 36.95) * mm});
            skSolve(sketch);
        }
        {
            var Q0;
            Q0=makeQuery(id+"F18.imprint","IMPRINT",FACE,{"disambiguationData":[TD([[makeQuery(id+"F18.imprint","IMPRINT",EDGE,{"derivedFrom":sQuery(id+"F18.wireOp",EDGE,"E62.bottom")}),-1.0]])]});
            extrude(context, id + "F19", {"entities" : qUnion([Q0]), "operationType" : NewBodyOperationType.ADD, "depth" : 20 * mm, "offsetDistance" : 25 * mm});
        }
        {
            var Q0;
            Q0=makeQuery(id+"F19.boolean.opBoolean","MERGE",FACE,{"derivedFrom":[makeQuery(id+"F1.opExtrude","SWEPT_FACE",FACE,{"disambiguationData":[OSD([sQuery(id+"F0.wireOp",EDGE,"E0.bottom")])]}),makeQuery(id+"F19.opExtrude","SWEPT_FACE",FACE,{"disambiguationData":[OSD([sQuery(id+"F18.wireOp",EDGE,"E62.bottom")])]})]});
            var sketch = newSketch(context, id + "F20", { "sketchPlane" : qUnion([Q0])});
            skCircle(sketch, "E63", {"center": v(-2.1, 20.09) * mm, "radius": 1.6 * mm});
            skCircle(sketch, "E64", {"center": v(21.9, 20.09) * mm, "radius": 1.6 * mm});
            skCircle(sketch, "E65", {"center": v(21.9, 9.93) * mm, "radius": 1.6 * mm});
            skCircle(sketch, "E66", {"center": v(-2.1, 10.09) * mm, "radius": 1.6 * mm});
            skSolve(sketch);
        }
        {
            var Q0;
            Q0 = qSketchRegion(id + "F20", true);
            extrude(context, id + "F21", {"entities" : qUnion([Q0]), "operationType" : NewBodyOperationType.REMOVE, "oppositeDirection" : true, "depth" : 10 * mm, "offsetDistance" : 25 * mm});
        }
    });
